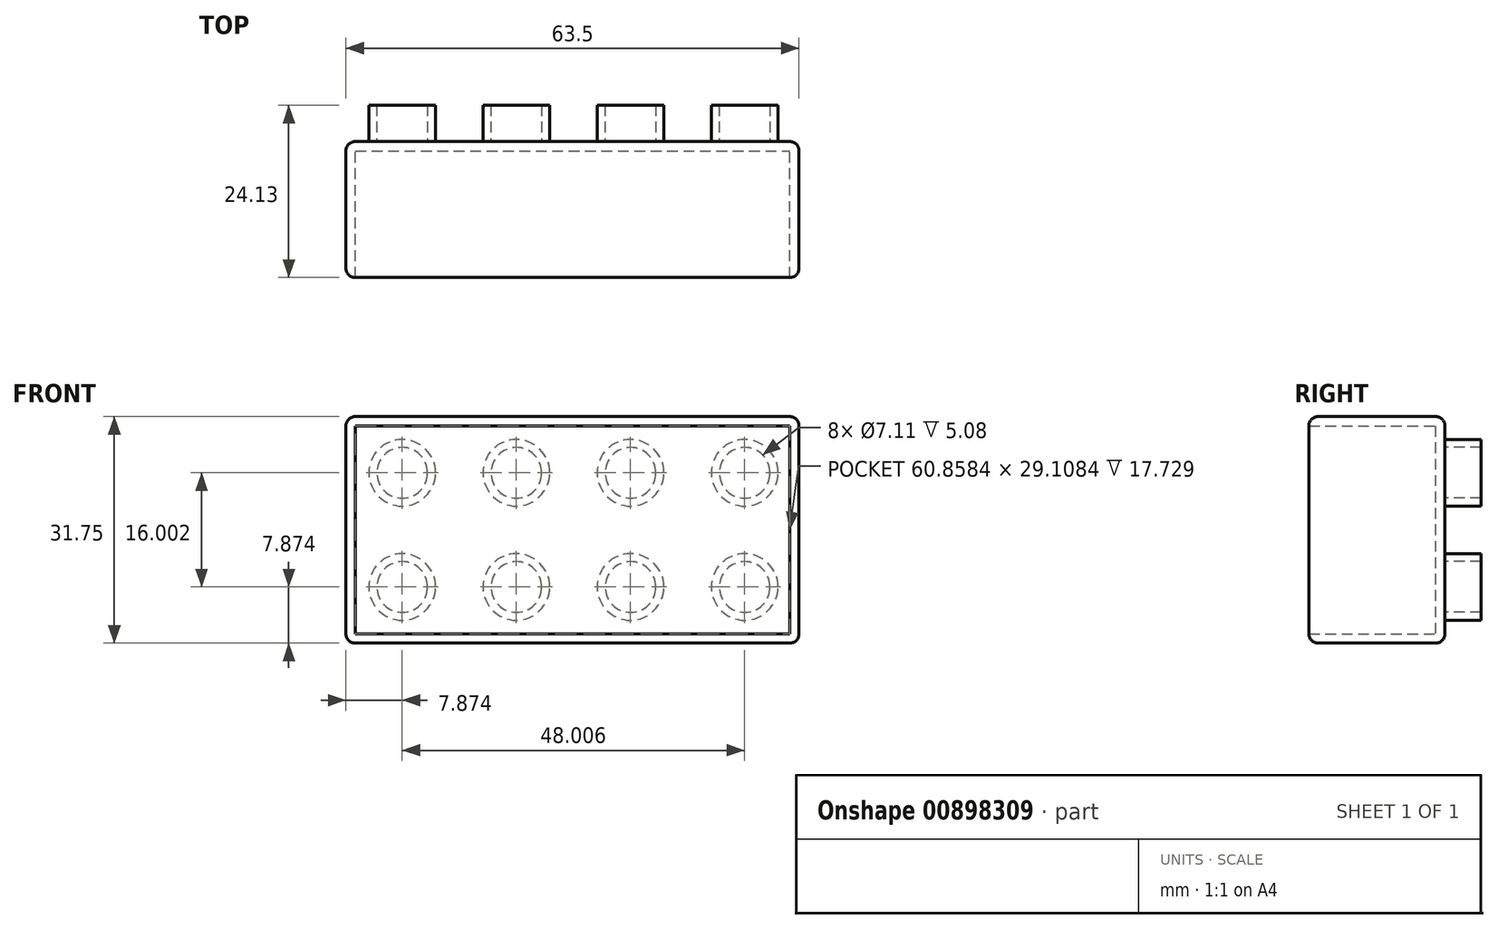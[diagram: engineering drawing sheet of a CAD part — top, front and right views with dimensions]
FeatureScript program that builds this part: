
annotation { "Feature Type Name" : "Feature", "Feature Type Description" : "" }
export const myFeature = defineFeature(function(context is Context, id is Id, definition is map)
    precondition{}
    {
        {
            var Q0;
            Q0=qCreatedBy(makeId("Top.planeOp"),FACE);
            var sketch = newSketch(context, id + "F0", { "sketchPlane" : qUnion([Q0])});
            skLineSegment(sketch, "E0.bottom", {"start": v(0, 0) * mm, "end": v(63.5, 0) * mm});
            skLineSegment(sketch, "E0.top", {"start": v(0, 19.05) * mm, "end": v(63.5, 19.05) * mm});
            skLineSegment(sketch, "E0.left", {"start": v(0, 0) * mm, "end": v(0, 19.05) * mm});
            skLineSegment(sketch, "E0.right", {"start": v(63.5, 0) * mm, "end": v(63.5, 19.05) * mm});
            skSolve(sketch);
        }
        {
            var Q0;
            Q0 = qSketchRegion(id + "F0", true);
            extrude(context, id + "F1", {"entities" : qUnion([Q0]), "depth" : 31.75 * mm, "offsetDistance" : 25.4 * mm});
        }
        {
            var Q0;
            Q0=makeQuery(id+"F1.opExtrude","SWEPT_FACE",FACE,{"disambiguationData":[OSD([sQuery(id+"F0.wireOp",EDGE,"E0.bottom")])]});
            shell(context, id + "F2", {"entities" : qUnion([Q0]), "thickness" : 1.32 * mm});
        }
        {
            var Q0;
            Q0=makeQuery(id+"F1.opExtrude","SWEPT_FACE",FACE,{"disambiguationData":[OSD([sQuery(id+"F0.wireOp",EDGE,"E0.top")])]});
            var sketch = newSketch(context, id + "F3", { "sketchPlane" : qUnion([Q0])});
            skCircle(sketch, "E1", {"center": v(-7.87, 23.88) * mm, "radius": 4.67 * mm});
            skCircle(sketch, "E2", {"center": v(-7.87, 23.88) * mm, "radius": 3.56 * mm});
            skCircle(sketch, "E3.1.0.0", {"center": v(-23.88, 23.88) * mm, "radius": 4.67 * mm});
            skCircle(sketch, "E3.1.0.1", {"center": v(-23.88, 23.88) * mm, "radius": 3.56 * mm});
            skCircle(sketch, "E3.2.0.0", {"center": v(-39.88, 23.88) * mm, "radius": 4.67 * mm});
            skCircle(sketch, "E3.2.0.1", {"center": v(-39.88, 23.88) * mm, "radius": 3.56 * mm});
            skCircle(sketch, "E3.3.0.0", {"center": v(-55.88, 23.88) * mm, "radius": 4.67 * mm});
            skCircle(sketch, "E3.3.0.1", {"center": v(-55.88, 23.88) * mm, "radius": 3.56 * mm});
            skLineSegment(sketch, "E3.direction1", {"start": v(-7.87, 23.88) * mm, "end": v(-23.88, 23.88) * mm, "construction": true});
            skCircle(sketch, "E4.1.0.0", {"center": v(-55.88, 7.87) * mm, "radius": 4.67 * mm});
            skCircle(sketch, "E4.1.0.1", {"center": v(-39.88, 7.87) * mm, "radius": 4.67 * mm});
            skCircle(sketch, "E4.1.0.2", {"center": v(-23.88, 7.87) * mm, "radius": 4.67 * mm});
            skCircle(sketch, "E4.1.0.3", {"center": v(-7.87, 7.87) * mm, "radius": 4.67 * mm});
            skCircle(sketch, "E4.1.0.4", {"center": v(-7.87, 7.87) * mm, "radius": 3.56 * mm});
            skCircle(sketch, "E4.1.0.5", {"center": v(-23.88, 7.87) * mm, "radius": 3.56 * mm});
            skCircle(sketch, "E4.1.0.6", {"center": v(-39.88, 7.87) * mm, "radius": 3.56 * mm});
            skCircle(sketch, "E4.1.0.7", {"center": v(-55.88, 7.87) * mm, "radius": 3.56 * mm});
            skLineSegment(sketch, "E4.direction1", {"start": v(-55.88, 23.88) * mm, "end": v(-55.88, 7.87) * mm, "construction": true});
            skSolve(sketch);
        }
        {
            var Q0;
            Q0 = qSketchRegion(id + "F3", true);
            extrude(context, id + "F4", {"entities" : qUnion([Q0]), "operationType" : NewBodyOperationType.ADD, "depth" : 5.08 * mm, "offsetDistance" : 25.4 * mm});
        }
        {
            var Q0;
            Q0=makeQuery(id+"F1.opExtrude","CAP_FACE",FACE,{"disambiguationData":[OSD([sQuery(id+"F0.wireOp",EDGE,"E0.bottom"),sQuery(id+"F0.wireOp",EDGE,"E0.top"),sQuery(id+"F0.wireOp",EDGE,"E0.left"),sQuery(id+"F0.wireOp",EDGE,"E0.right")])],"isStart":false});
            var Q1;
            Q1=makeQuery(id+"F1.opExtrude","SWEPT_FACE",FACE,{"disambiguationData":[OSD([sQuery(id+"F0.wireOp",EDGE,"E0.left")])]});
            var Q2;
            Q2=makeQuery(id+"F1.opExtrude","CAP_FACE",FACE,{"disambiguationData":[OSD([sQuery(id+"F0.wireOp",EDGE,"E0.bottom"),sQuery(id+"F0.wireOp",EDGE,"E0.top"),sQuery(id+"F0.wireOp",EDGE,"E0.left"),sQuery(id+"F0.wireOp",EDGE,"E0.right")])],"isStart":true});
            var Q3;
            Q3=makeQuery(id+"F1.opExtrude","SWEPT_FACE",FACE,{"disambiguationData":[OSD([sQuery(id+"F0.wireOp",EDGE,"E0.right")])]});
            fillet(context, id + "F5", {"entities" : qUnion([Q0, Q1, Q2, Q3]), "radius" : 1.27 * mm, "tangentPropagation" : true, "allowEdgeOverflow" : false});
        }
    });
